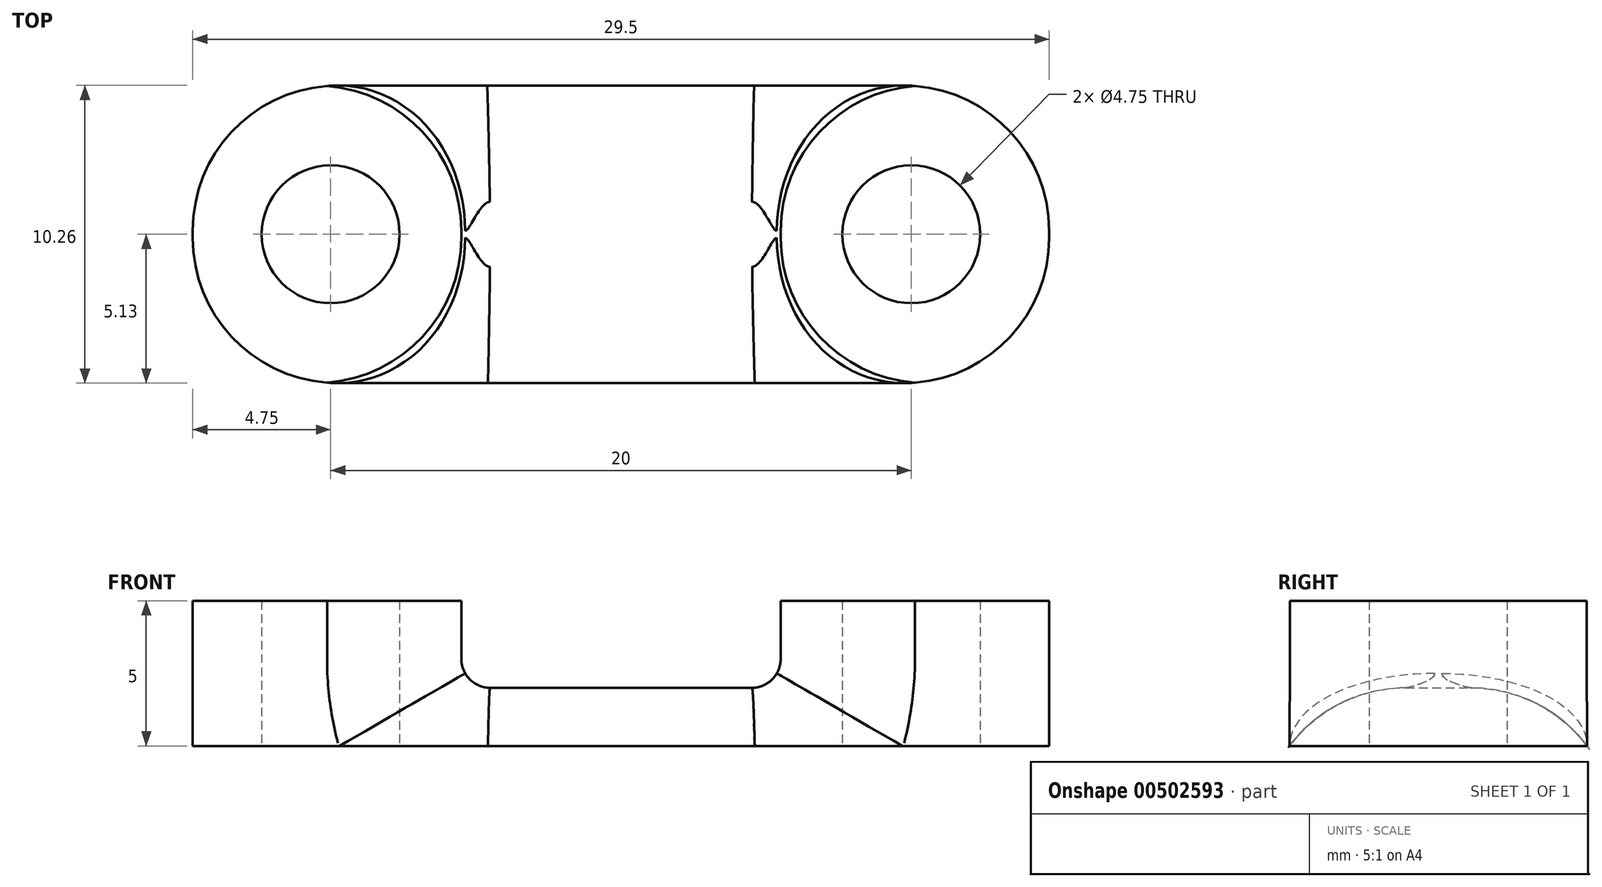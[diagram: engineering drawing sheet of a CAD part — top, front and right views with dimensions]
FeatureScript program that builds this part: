
annotation { "Feature Type Name" : "Feature", "Feature Type Description" : "" }
export const myFeature = defineFeature(function(context is Context, id is Id, definition is map)
    precondition{}
    {
        {
            var Q0;
            Q0=qCreatedBy(makeId("Top.planeOp"),FACE);
            var sketch = newSketch(context, id + "F0", { "sketchPlane" : qUnion([Q0])});
            skLineSegment(sketch, "E0.bottom", {"start": v(13.25, -5.12) * mm, "end": v(-13.25, -5.13) * mm});
            skLineSegment(sketch, "E0.top", {"start": v(13.25, 5.13) * mm, "end": v(-13.25, 5.12) * mm});
            skLineSegment(sketch, "E0.left", {"start": v(14.75, -3.62) * mm, "end": v(14.75, 3.63) * mm});
            skLineSegment(sketch, "E0.right", {"start": v(-14.75, -3.63) * mm, "end": v(-14.75, 3.62) * mm});
            skPoint(sketch, "E0.middle", {"position": v(0, 0) * mm});
            skLineSegment(sketch, "E1", {"start": v(0, 0) * mm, "end": v(10, 0) * mm});
            skLineSegment(sketch, "E2", {"start": v(0, 0) * mm, "end": v(-10, 0) * mm});
            skCircle(sketch, "E3", {"center": v(10, 0) * mm, "radius": 2.38 * mm});
            skCircle(sketch, "E4", {"center": v(-10, 0) * mm, "radius": 2.38 * mm});
            skPoint(sketch, "E5.visualSharp", {"position": v(-14.75, 5.12) * mm});
            skPoint(sketch, "E6.visualSharp", {"position": v(-14.75, -5.13) * mm});
            skPoint(sketch, "E7.visualSharp", {"position": v(14.75, -5.12) * mm});
            skPoint(sketch, "E8.visualSharp", {"position": v(14.75, 5.13) * mm});
            skLineSegment(sketch, "E9", {"start": v(-13.25, -5.13) * mm, "end": v(-14.75, -5.13) * mm});
            skLineSegment(sketch, "E10", {"start": v(-14.75, -3.63) * mm, "end": v(-14.75, -5.13) * mm});
            skLineSegment(sketch, "E11", {"start": v(-13.25, 5.12) * mm, "end": v(-14.75, 5.12) * mm});
            skLineSegment(sketch, "E12", {"start": v(-14.75, 3.62) * mm, "end": v(-14.75, 5.12) * mm});
            skLineSegment(sketch, "E13", {"start": v(13.25, 5.13) * mm, "end": v(14.75, 5.13) * mm});
            skLineSegment(sketch, "E14", {"start": v(14.75, 3.63) * mm, "end": v(14.75, 5.13) * mm});
            skLineSegment(sketch, "E15", {"start": v(14.75, -3.62) * mm, "end": v(14.75, -5.12) * mm});
            skLineSegment(sketch, "E16", {"start": v(14.75, -5.12) * mm, "end": v(13.25, -5.12) * mm});
            skSolve(sketch);
        }
        {
            var Q0;
            Q0=makeQuery(id+"F0.imprint","IMPRINT",FACE,{"disambiguationData":[TD([[makeQuery(id+"F0.imprint","IMPRINT",EDGE,{"derivedFrom":sQuery(id+"F0.wireOp",EDGE,"E0.bottom")}),-1.0]])]});
            extrude(context, id + "F1", {"entities" : qUnion([Q0]), "depth" : 5 * mm});
        }
        {
            var Q0;
            Q0=qCreatedBy(makeId("Front.planeOp"),FACE);
            var sketch = newSketch(context, id + "F2", { "sketchPlane" : qUnion([Q0])});
            skLineSegment(sketch, "E17", {"start": v(0, 0) * mm, "end": v(0, 4.5) * mm});
            skLineSegment(sketch, "E18.bottom", {"start": v(4.5, 2) * mm, "end": v(-4.5, 2) * mm});
            skLineSegment(sketch, "E18.top", {"start": v(5.5, 7) * mm, "end": v(-5.5, 7) * mm});
            skLineSegment(sketch, "E18.left", {"start": v(5.5, 3) * mm, "end": v(5.5, 7) * mm});
            skLineSegment(sketch, "E18.right", {"start": v(-5.5, 3) * mm, "end": v(-5.5, 7) * mm});
            skPoint(sketch, "E18.middle", {"position": v(0, 4.5) * mm});
            skPoint(sketch, "E19.visualSharp", {"position": v(5.5, 2) * mm});
            skArc(sketch, "E19.filletArc", {"start": v(4.5, 2) * mm, "mid": v(5.2, 2.3) * mm, "end": v(5.5, 3) * mm});
            skPoint(sketch, "E20.visualSharp", {"position": v(-5.5, 2) * mm});
            skArc(sketch, "E20.filletArc", {"start": v(-5.5, 3) * mm, "mid": v(-5.2, 2.3) * mm, "end": v(-4.5, 2) * mm});
            skSolve(sketch);
        }
        {
            var Q0;
            Q0=makeQuery(id+"F2.imprint","IMPRINT",FACE,{"disambiguationData":[TD([[makeQuery(id+"F2.imprint","IMPRINT",EDGE,{"derivedFrom":sQuery(id+"F2.wireOp",EDGE,"E18.top")}),1.0]])]});
            extrude(context, id + "F3", {"entities" : qUnion([Q0]), "operationType" : NewBodyOperationType.REMOVE, "depth" : 10 * mm, "hasSecondDirection" : true, "secondDirectionOppositeDirection" : true, "secondDirectionDepth" : 10 * mm});
        }
        {
            var Q0;
            Q0=makeQuery(id+"F3.boolean.opBoolean","INTERSECT",EDGE,{"derivedFrom":[makeQuery(id+"F1.opExtrude","SWEPT_FACE",FACE,{"disambiguationData":[OSD([sQuery(id+"F0.wireOp",EDGE,"E0.bottom")])]}),makeQuery(id+"F3.opExtrude","SWEPT_FACE",FACE,{"disambiguationData":[OSD([sQuery(id+"F2.wireOp",EDGE,"E18.left")])]})]});
            fillet(context, id + "F4", {"entities" : qUnion([Q0]), "radius" : 5 * mm, "tangentPropagation" : true, "allowEdgeOverflow" : false});
        }
        {
            var Q0;
            Q0=makeQuery(id+"F3.boolean.opBoolean","INTERSECT",EDGE,{"derivedFrom":[makeQuery(id+"F1.opExtrude","SWEPT_FACE",FACE,{"disambiguationData":[OSD([sQuery(id+"F0.wireOp",EDGE,"E0.top")])]}),makeQuery(id+"F3.opExtrude","SWEPT_FACE",FACE,{"disambiguationData":[OSD([sQuery(id+"F2.wireOp",EDGE,"E18.right")])]})]});
            fillet(context, id + "F5", {"entities" : qUnion([Q0]), "radius" : 5 * mm, "tangentPropagation" : true, "allowEdgeOverflow" : false});
        }
        {
            var Q0;
            Q0=makeQuery(id+"F1.opExtrude","SWEPT_EDGE",EDGE,{"disambiguationData":[OSD([sQuery(id+"F0.wireOp",EDGE,"E9"),sQuery(id+"F0.wireOp",EDGE,"E10")])]});
            var Q1;
            Q1=makeQuery(id+"F1.opExtrude","SWEPT_EDGE",EDGE,{"disambiguationData":[OSD([sQuery(id+"F0.wireOp",EDGE,"E11"),sQuery(id+"F0.wireOp",EDGE,"E12")])]});
            var Q2;
            Q2=makeQuery(id+"F1.opExtrude","SWEPT_EDGE",EDGE,{"disambiguationData":[OSD([sQuery(id+"F0.wireOp",EDGE,"E15"),sQuery(id+"F0.wireOp",EDGE,"E16")])]});
            var Q3;
            Q3=makeQuery(id+"F1.opExtrude","SWEPT_EDGE",EDGE,{"disambiguationData":[OSD([sQuery(id+"F0.wireOp",EDGE,"E13"),sQuery(id+"F0.wireOp",EDGE,"E14")])]});
            fillet(context, id + "F6", {"entities" : qUnion([Q0, Q1, Q2, Q3]), "radius" : 5 * mm, "tangentPropagation" : true, "allowEdgeOverflow" : false});
        }
    });
